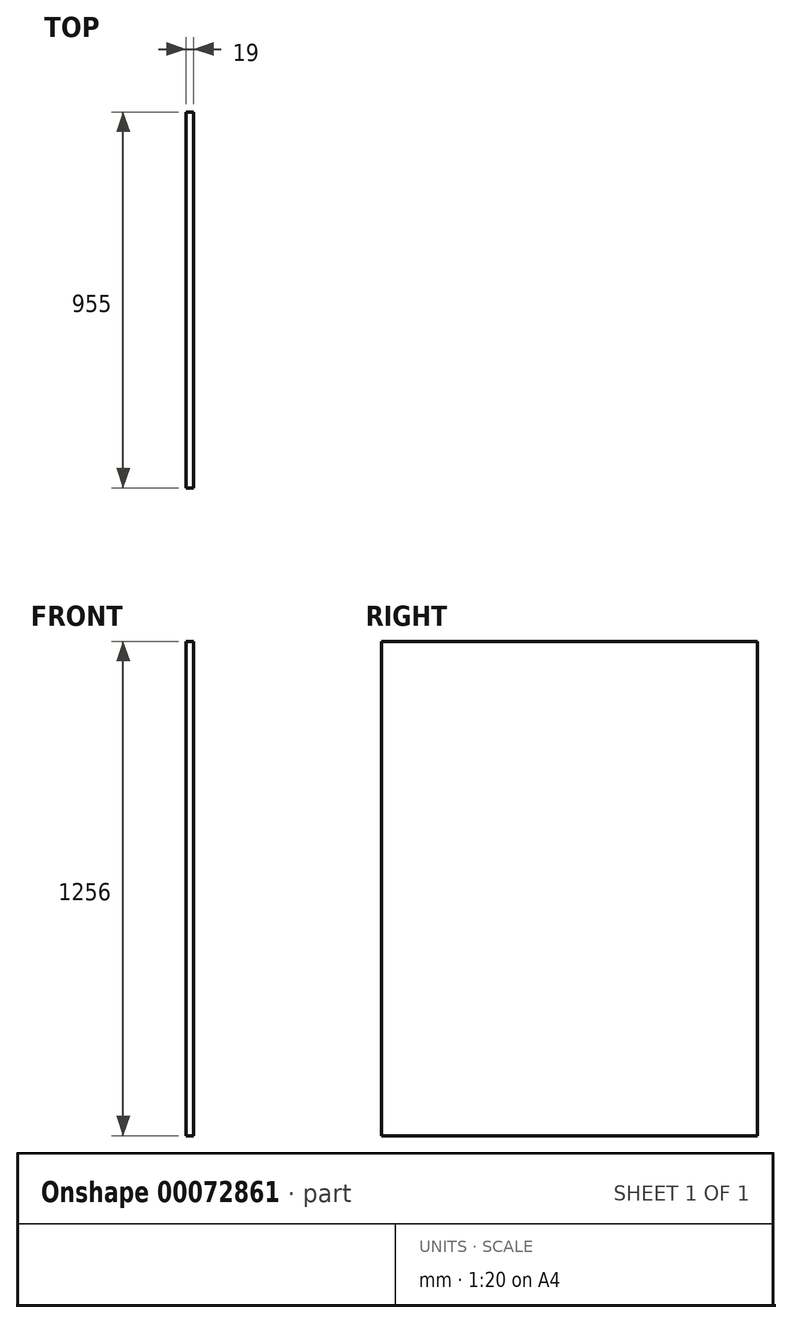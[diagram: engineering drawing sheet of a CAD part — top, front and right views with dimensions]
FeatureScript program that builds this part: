
annotation { "Feature Type Name" : "Feature", "Feature Type Description" : "" }
export const myFeature = defineFeature(function(context is Context, id is Id, definition is map)
    precondition{}
    {
        {
            var Q0;
            Q0=qCreatedBy(makeId("Right.planeOp"),FACE);
            var sketch = newSketch(context, id + "F0", { "sketchPlane" : qUnion([Q0])});
            skLineSegment(sketch, "E0.bottom", {"start": v(-474.52, 455.16) * mm, "end": v(480.48, 455.16) * mm});
            skLineSegment(sketch, "E0.top", {"start": v(-474.52, -800.84) * mm, "end": v(480.48, -800.84) * mm});
            skLineSegment(sketch, "E0.left", {"start": v(-474.52, 455.16) * mm, "end": v(-474.52, -800.84) * mm});
            skLineSegment(sketch, "E0.right", {"start": v(480.48, 455.16) * mm, "end": v(480.48, -800.84) * mm});
            skSolve(sketch);
        }
        {
            var Q0;
            Q0=makeQuery(id+"F0.imprint","IMPRINT",FACE,{"disambiguationData":[TD([[makeQuery(id+"F0.imprint","IMPRINT",EDGE,{"derivedFrom":sQuery(id+"F0.wireOp",EDGE,"E0.bottom")}),-1.0]])]});
            extrude(context, id + "F1", {"entities" : qUnion([Q0]), "depth" : 19 * mm});
        }
    });
